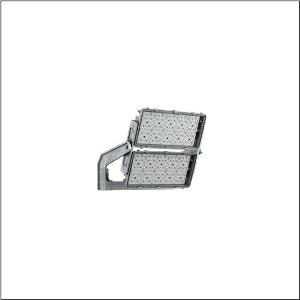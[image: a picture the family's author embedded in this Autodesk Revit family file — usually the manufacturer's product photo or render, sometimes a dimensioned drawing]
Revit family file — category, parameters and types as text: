
# Revit family: floodlight_fl_11_maxi_remote___rs12_5xa779514m01ba_3a09
name_source: partatom
category: Lighting Fixtures
units: mm (PartAtom-declared; Revit-internal decimal feet)

## family parameters
Cut with Voids When Loaded = No
Host = Face
Light Source = No
Part Type = Normal
Room Calculation Point = No
Round Connector Dimension = Use Diameter
Shared = No

## types (1)
- --- (1 x LED, 76660 lm, 707.9 W, 5700K)
    Apparent Load = 708 VA
    CIE Flux Codes = 79 92 99 100 100
    Color Rendering = 90
    Color Temperature = 5700K
    Default Elevation = 1800 mm
    Description = Floodlight FL 11  maxi  Remote floodlight; light control with lens of PMMA; cover panel of toughened safety glass, transparent; light distribution: RS12, rotationally symmetric direct distribution, LEDcolour temperature: 5700K, rated luminous flux: 76.660lm, colour rendering: CRI > 90, light colour: 957; luminous efficacy: 108lm/W; brightness control: DMX+RDM; with terminal, 8-pole, max. 2.5mm², mains connection: 220..240V/380..400V AC, 50/60Hz, surge voltage resistance: line to ground: 10kV, ECG replaceable separately, LED unit replaceable without ESD environment, dustproof LED module, dimming range 10..100%; 708W floodlight with 2x LED unit of diecast aluminium, coated grey; length: 713mm / width: 651mm / height: 338mm; mounting bracket, of diecast aluminium, uncoated, natural, equipment: Longlife, protection rating (complete): IP66; insulation class (complete): insulation class I (protective earthing); certification: CE, ENEC, VDE; ball protection: ball impact resistance with accessories, impact resistance: IK07; only for outdoor installations, rated ambient temperature 10°C, permissible operating ambient temperature: -40..+40°C, permissible storage temperature: -40..+85°C; packaging unit: 1 piece

Light Distribution: RS12
    Height = 320 mm
    Lamp = 1 x LED
    Lamp Light Flux = 76660 lm
    Lamp Power = 707.9 W
    Lamp count = 1
    Length = 712 mm
    Luminous efficacy = 108 lm/W
    Manufacturer = Siteco
    ModVariant = No
    Model = 5XA779514M01BA
    Mounting Place = Ceiling
    Mounting Type = Surface mounted
    Number of Poles = 1
    OnlyDefault = Yes
    Power Factor = 1
    Product Name = Floodlight FL 11 maxi Remote | RS12
    Product group = floodlight | ceiling mounted
    ProductGroupID = 302
    Protection Class = Protection class I
    Protection Degree = IP 66
    RLX_Detail_Level = 1
    RLX_Emergency_Light_Flux = 0 lm
    RLX_Emergency_Type = 0
    RLX_Emergency_Type_DB = No
    RlxData = <blob elided: 41093 chars, md5=6009f514>
    Socket = socket
    Standby Power = 0 W
    System Light Flux = 76660 lm
    System Power = 708 W
    Type Comments = factory setting: luminous flux: 100 % | dim-lin: 254 | 740 mA
    Type Image = l_1006788.jpg
    URL = http://relux.com
    VarID = @adj_153595
    Voltage = 0 V
    Weight = 0.00 kg
    Width = 655 mm

## geometry (parser evidence)
native form markers: Blend x4, Sweep x14
no freeform markers — native parametric forms only
